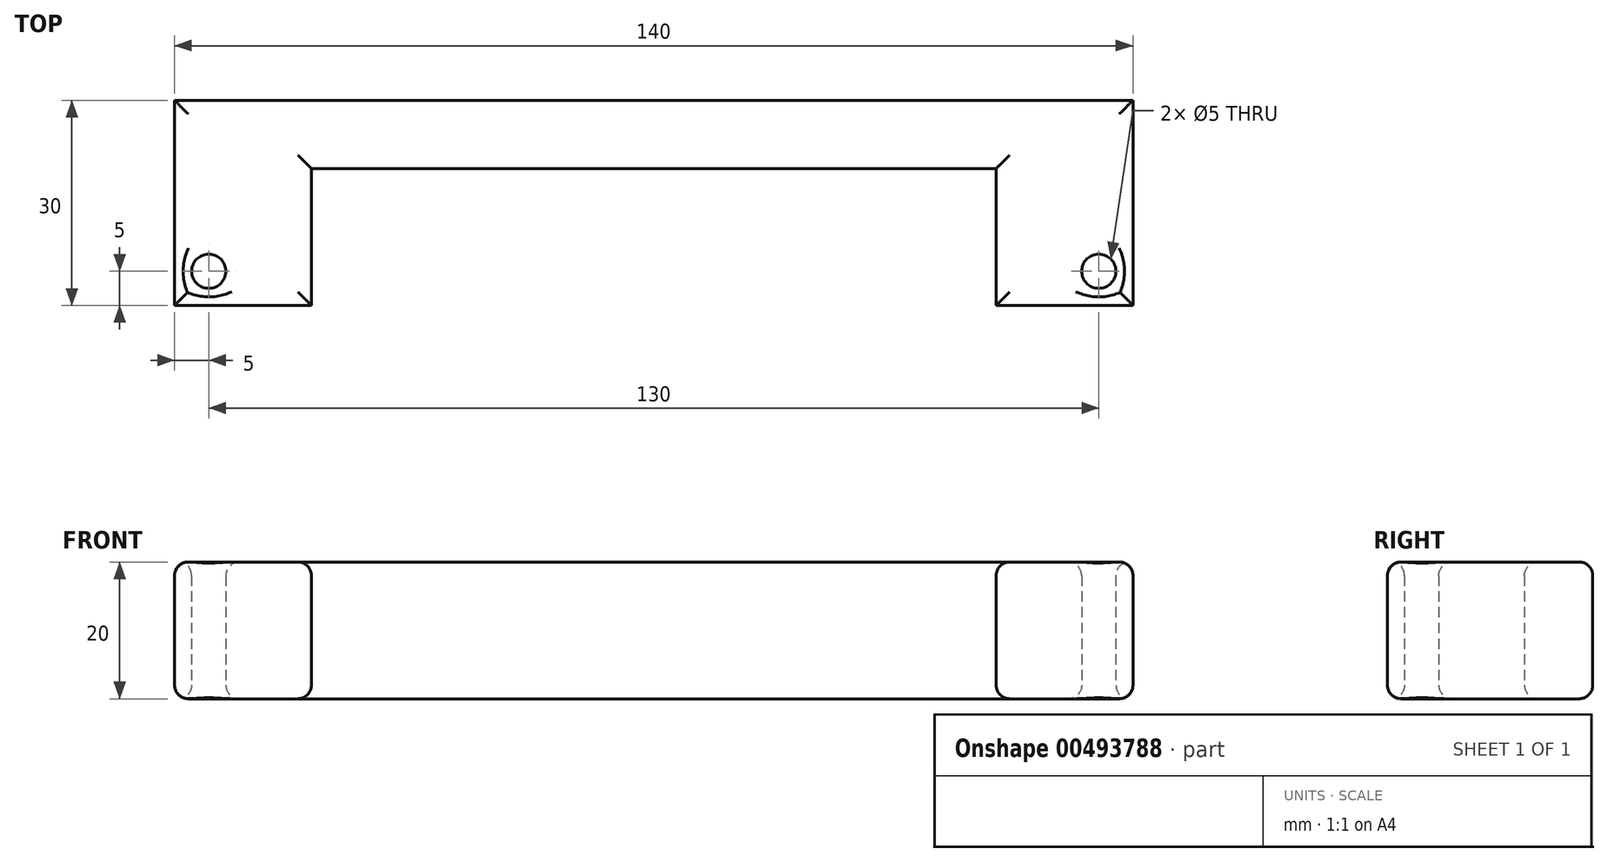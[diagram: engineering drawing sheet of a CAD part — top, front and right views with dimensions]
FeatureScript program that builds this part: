
annotation { "Feature Type Name" : "Feature", "Feature Type Description" : "" }
export const myFeature = defineFeature(function(context is Context, id is Id, definition is map)
    precondition{}
    {
        {
            var Q0;
            Q0=qCreatedBy(makeId("Top.planeOp"),FACE);
            var sketch = newSketch(context, id + "F0", { "sketchPlane" : qUnion([Q0])});
            skLineSegment(sketch, "E0", {"start": v(0, 30) * mm, "end": v(70, 30) * mm});
            skLineSegment(sketch, "E1", {"start": v(70, 30) * mm, "end": v(70, 0) * mm});
            skLineSegment(sketch, "E2", {"start": v(70, 0) * mm, "end": v(50, 0) * mm});
            skLineSegment(sketch, "E3", {"start": v(50, 0) * mm, "end": v(50, 20) * mm});
            skLineSegment(sketch, "E4", {"start": v(50, 20) * mm, "end": v(0, 20) * mm});
            skLineSegment(sketch, "E5", {"start": v(0, 20) * mm, "end": v(0, 30) * mm});
            skSolve(sketch);
        }
        {
            var Q0;
            Q0 = qSketchRegion(id + "F0", true);
            extrude(context, id + "F1", {"entities" : qUnion([Q0]), "depth" : 20 * mm});
        }
        {
            var Q0;
            Q0=qCreatedBy(makeId("Top.planeOp"),FACE);
            var sketch = newSketch(context, id + "F2", { "sketchPlane" : qUnion([Q0])});
            skPoint(sketch, "E6", {"position": v(65, 5) * mm});
            skSolve(sketch);
        }
        {
            var Q0;
            Q0=sQuery(id+"F2.wireOp",VERTEX,"E6");
            var Q1;
            Q1=makeQuery(id+"F1.opExtrude","SWEPT_BODY",BODY,{"disambiguationData":[OSD([sQuery(id+"F0.wireOp",EDGE,"E0"),sQuery(id+"F0.wireOp",EDGE,"E1"),sQuery(id+"F0.wireOp",EDGE,"E2"),sQuery(id+"F0.wireOp",EDGE,"E3"),sQuery(id+"F0.wireOp",EDGE,"E4"),sQuery(id+"F0.wireOp",EDGE,"E5")])]});
            hole(context, id + "F3", {"style" : HoleStyle.SIMPLE, "endStyle" : HoleEndStyle.THROUGH, "oppositeDirection" : true, "holeDiameter" : 5 * mm, "isTappedThrough" : true, "tappedDepth" : 12 * mm, "tapClearance" : 3, "locations" : qUnion([Q0]), "scope" : qUnion([Q1])});
        }
        {
            var Q0;
            Q0=makeQuery(id+"F1.opExtrude","SWEPT_BODY",BODY,{"disambiguationData":[OSD([sQuery(id+"F0.wireOp",EDGE,"E0"),sQuery(id+"F0.wireOp",EDGE,"E1"),sQuery(id+"F0.wireOp",EDGE,"E2"),sQuery(id+"F0.wireOp",EDGE,"E3"),sQuery(id+"F0.wireOp",EDGE,"E4"),sQuery(id+"F0.wireOp",EDGE,"E5")])]});
            var Q1;
            Q1=makeQuery(id+"F1.opExtrude","SWEPT_FACE",FACE,{"disambiguationData":[OSD([sQuery(id+"F0.wireOp",EDGE,"E5")])]});
            mirror(context, id + "F4", {"operationType" : NewBodyOperationType.ADD, "entities" : qUnion([Q0]), "mirrorPlane" : qUnion([Q1])});
        }
        {
            var Q0;
            {var subQ0=makeQuery(id+"F1.opExtrude","CAP_FACE",FACE,{"disambiguationData":[OSD([sQuery(id+"F0.wireOp",EDGE,"E0"),sQuery(id+"F0.wireOp",EDGE,"E1"),sQuery(id+"F0.wireOp",EDGE,"E2"),sQuery(id+"F0.wireOp",EDGE,"E3"),sQuery(id+"F0.wireOp",EDGE,"E4"),sQuery(id+"F0.wireOp",EDGE,"E5")])],"isStart":false});Q0=makeQuery(id+"F4.boolean.opBoolean","MERGE",FACE,{"derivedFrom":[subQ0,makeQuery(id+"F4.opPattern","COPY",FACE,{"derivedFrom":subQ0,"instanceName":"1"})]});}
            fillet(context, id + "F5", {"entities" : qUnion([Q0]), "radius" : 2 * mm, "tangentPropagation" : true, "allowEdgeOverflow" : false});
        }
        {
            var Q0;
            {var subQ0=makeQuery(id+"F1.opExtrude","CAP_FACE",FACE,{"disambiguationData":[OSD([sQuery(id+"F0.wireOp",EDGE,"E0"),sQuery(id+"F0.wireOp",EDGE,"E1"),sQuery(id+"F0.wireOp",EDGE,"E2"),sQuery(id+"F0.wireOp",EDGE,"E3"),sQuery(id+"F0.wireOp",EDGE,"E4"),sQuery(id+"F0.wireOp",EDGE,"E5")])],"isStart":true});Q0=makeQuery(id+"F4.boolean.opBoolean","MERGE",FACE,{"derivedFrom":[subQ0,makeQuery(id+"F4.opPattern","COPY",FACE,{"derivedFrom":subQ0,"instanceName":"1"})]});}
            fillet(context, id + "F6", {"entities" : qUnion([Q0]), "radius" : 2 * mm, "tangentPropagation" : true, "allowEdgeOverflow" : false});
        }
    });
